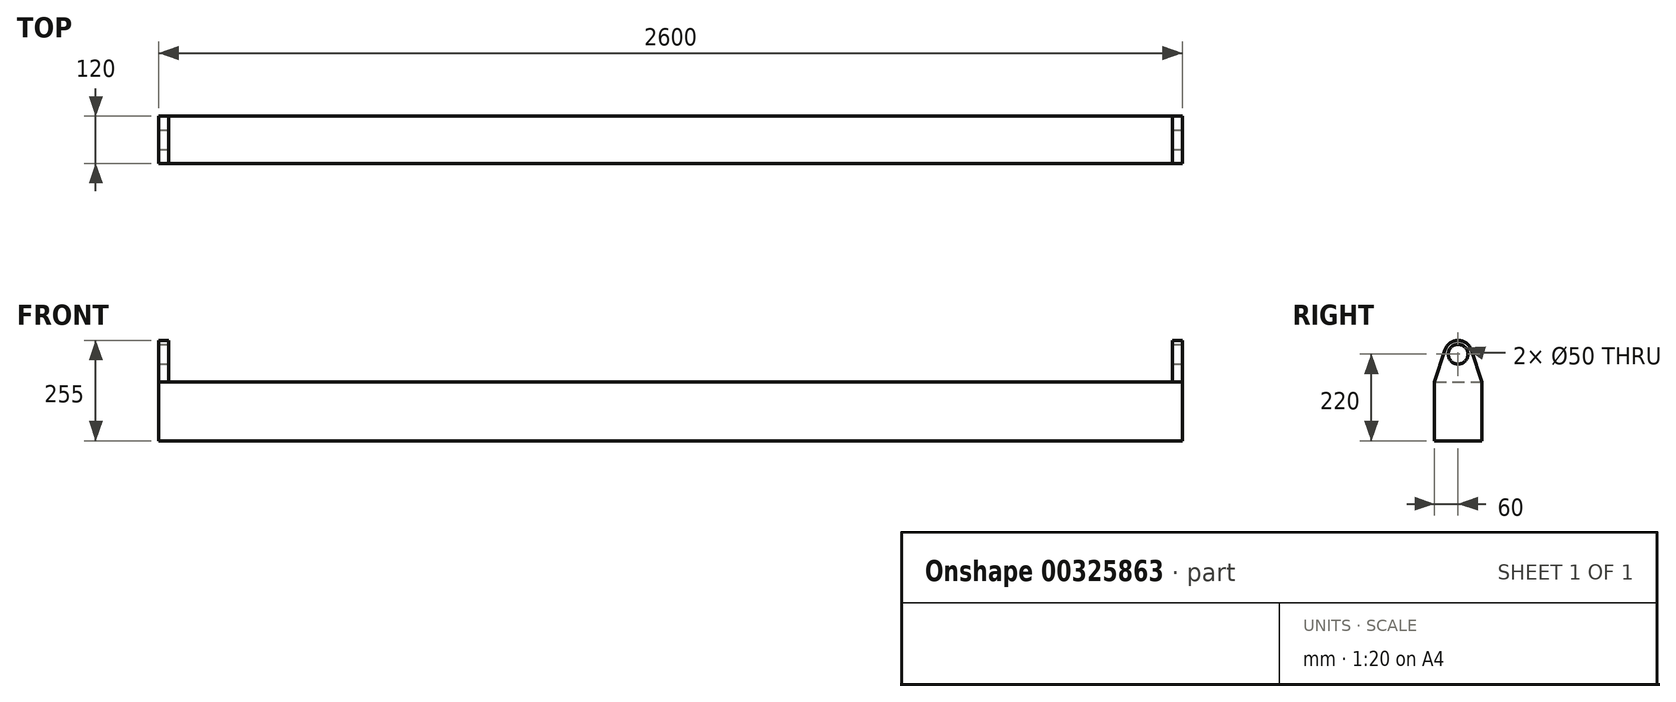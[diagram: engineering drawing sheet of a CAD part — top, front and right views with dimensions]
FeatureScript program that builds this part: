
annotation { "Feature Type Name" : "Feature", "Feature Type Description" : "" }
export const myFeature = defineFeature(function(context is Context, id is Id, definition is map)
    precondition{}
    {
        {
            var Q0;
            Q0=qCreatedBy(makeId("Top.planeOp"),FACE);
            var sketch = newSketch(context, id + "F0", { "sketchPlane" : qUnion([Q0])});
            skLineSegment(sketch, "E0.bottom", {"start": v(0, 0) * mm, "end": v(2600, 0) * mm});
            skLineSegment(sketch, "E0.top", {"start": v(0, 120) * mm, "end": v(2600, 120) * mm});
            skLineSegment(sketch, "E0.left", {"start": v(0, 0) * mm, "end": v(0, 120) * mm});
            skLineSegment(sketch, "E0.right", {"start": v(2600, 0) * mm, "end": v(2600, 120) * mm});
            skSolve(sketch);
        }
        {
            var Q0;
            Q0=makeQuery(id+"F0.imprint","IMPRINT",FACE,{"disambiguationData":[TD([[makeQuery(id+"F0.imprint","IMPRINT",EDGE,{"derivedFrom":sQuery(id+"F0.wireOp",EDGE,"E0.bottom")}),1.0]])]});
            extrude(context, id + "F1", {"entities" : qUnion([Q0]), "depth" : 150 * mm});
        }
        {
            var Q0;
            Q0=qCreatedBy(makeId("Right.planeOp"),FACE);
            var sketch = newSketch(context, id + "F2", { "sketchPlane" : qUnion([Q0])});
            skLineSegment(sketch, "E1", {"start": v(0, 150) * mm, "end": v(120, 150) * mm});
            skArc(sketch, "E2", {"start": v(93.23, 230.98) * mm, "mid": v(60, 255) * mm, "end": v(26.77, 230.98) * mm});
            skLineSegment(sketch, "E3", {"start": v(0, 150) * mm, "end": v(26.77, 230.98) * mm});
            skLineSegment(sketch, "E4", {"start": v(120, 150) * mm, "end": v(93.23, 230.98) * mm});
            skSolve(sketch);
        }
        {
            var Q0;
            Q0=makeQuery(id+"F2.imprint","IMPRINT",FACE,{"disambiguationData":[TD([[makeQuery(id+"F2.imprint","IMPRINT",EDGE,{"derivedFrom":sQuery(id+"F2.wireOp",EDGE,"E1")}),1.0]])]});
            extrude(context, id + "F3", {"entities" : qUnion([Q0]), "operationType" : NewBodyOperationType.ADD, "depth" : 25 * mm});
        }
        {
            var Q0;
            Q0=makeQuery(id+"F1.opExtrude","SWEPT_FACE",FACE,{"disambiguationData":[OSD([sQuery(id+"F0.wireOp",EDGE,"E0.right")])]});
            var sketch = newSketch(context, id + "F4", { "sketchPlane" : qUnion([Q0])});
            skLineSegment(sketch, "E5", {"start": v(0, 150) * mm, "end": v(120, 150) * mm});
            skArc(sketch, "E6", {"start": v(93.23, 230.98) * mm, "mid": v(60, 255) * mm, "end": v(26.77, 230.98) * mm});
            skLineSegment(sketch, "E7", {"start": v(0, 150) * mm, "end": v(26.77, 230.98) * mm});
            skLineSegment(sketch, "E8", {"start": v(120, 150) * mm, "end": v(93.23, 230.98) * mm});
            skSolve(sketch);
        }
        {
            var Q0;
            Q0=makeQuery(id+"F4.imprint","IMPRINT",FACE,{"disambiguationData":[TD([[makeQuery(id+"F4.imprint","IMPRINT",EDGE,{"derivedFrom":sQuery(id+"F4.wireOp",EDGE,"E5")}),1.0]])]});
            extrude(context, id + "F5", {"entities" : qUnion([Q0]), "oppositeDirection" : true, "depth" : 25 * mm});
        }
        {
            var Q0;
            Q0=makeQuery(id+"F1.opExtrude","SWEPT_BODY",BODY,{"disambiguationData":[OSD([sQuery(id+"F0.wireOp",EDGE,"E0.bottom"),sQuery(id+"F0.wireOp",EDGE,"E0.top"),sQuery(id+"F0.wireOp",EDGE,"E0.left"),sQuery(id+"F0.wireOp",EDGE,"E0.right")])]});
            var Q1;
            Q1=makeQuery(id+"F5.opExtrude","SWEPT_BODY",BODY,{"disambiguationData":[OSD([sQuery(id+"F4.wireOp",EDGE,"E5"),sQuery(id+"F4.wireOp",EDGE,"E6"),sQuery(id+"F4.wireOp",EDGE,"E7"),sQuery(id+"F4.wireOp",EDGE,"E8")])]});
            booleanBodies(context, id + "F6", {"operationType" : BooleanOperationType.UNION, "tools" : qUnion([Q0, Q1])});
        }
        {
            var Q0;
            Q0=makeQuery(id+"F6.opBoolean","MERGE",FACE,{"derivedFrom":[makeQuery(id+"F1.opExtrude","SWEPT_FACE",FACE,{"disambiguationData":[OSD([sQuery(id+"F0.wireOp",EDGE,"E0.right")])]}),makeQuery(id+"F5.opExtrude","CAP_FACE",FACE,{"disambiguationData":[OSD([sQuery(id+"F4.wireOp",EDGE,"E5"),sQuery(id+"F4.wireOp",EDGE,"E6"),sQuery(id+"F4.wireOp",EDGE,"E7"),sQuery(id+"F4.wireOp",EDGE,"E8")])],"isStart":true})]});
            var sketch = newSketch(context, id + "F7", { "sketchPlane" : qUnion([Q0])});
            skCircle(sketch, "E9", {"center": v(60, 220) * mm, "radius": 25 * mm});
            skSolve(sketch);
        }
        {
            var Q0;
            Q0=makeQuery(id+"F7.imprint","IMPRINT",FACE,{"disambiguationData":[TD([[makeQuery(id+"F7.imprint","IMPRINT",EDGE,{"derivedFrom":sQuery(id+"F7.wireOp",EDGE,"E9")}),1.0]])]});
            extrude(context, id + "F8", {"entities" : qUnion([Q0]), "operationType" : NewBodyOperationType.REMOVE, "oppositeDirection" : true, "depth" : 3000 * mm});
        }
    });
